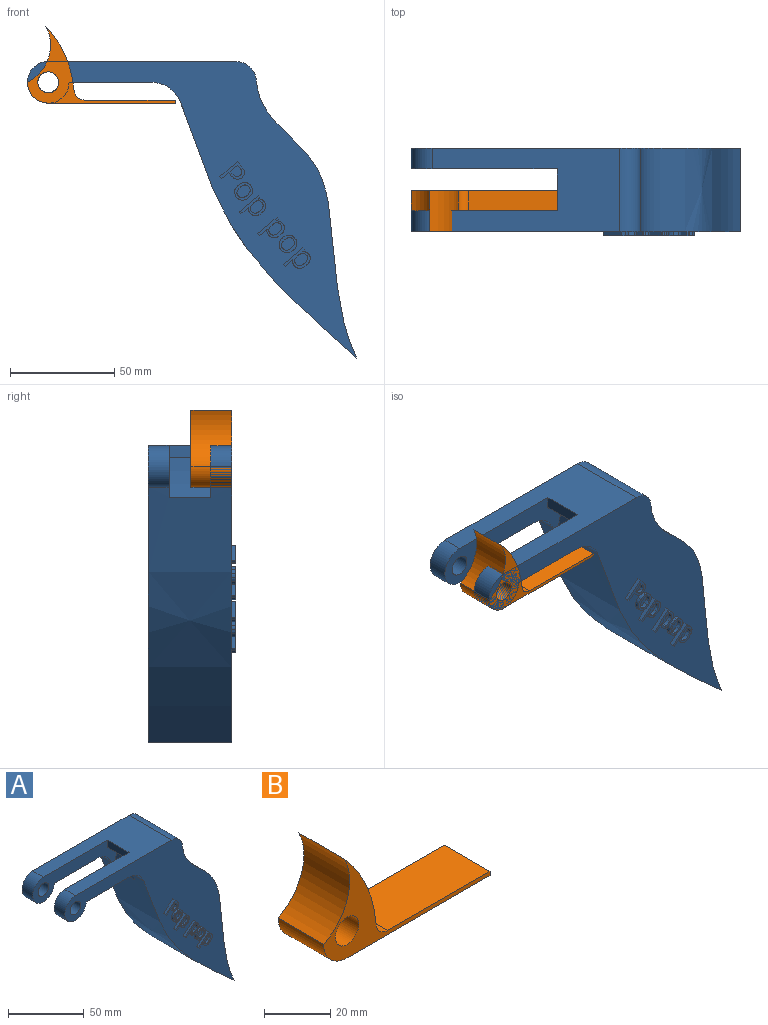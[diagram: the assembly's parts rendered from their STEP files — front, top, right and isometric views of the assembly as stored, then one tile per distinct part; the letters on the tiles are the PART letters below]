
ASSEMBLY  parts=2 mates=1
PART A: 155 faces, bbox 158.1x42x142.4 mm
  f0: cylinder r=70mm len=20mm, axis (0,1,0), area 390.4mm2, adj f1,f6,f12,f18
  f1: extruded ~122.5x84.4mm, area 5962.1mm2, adj f0,f2,f7,f10,f12,f13,f16,f18
  f2: extruded ~132.4x48.08mm, area 5806.9mm2, adj f1,f3,f7,f13
  f3: cylinder r=10mm len=40mm, axis (0,1,0), area 628.3mm2, adj f2,f4,f7,f13
  f4: plane 90x40mm, normal (0,0,1), area 2400mm2, adj f3,f5,f7,f8,f12,f13,f14,f18
  f5: plane 20x5.86mm, normal (-1,0,0), area 117.2mm2, adj f4,f6,f12,f18
  f6: plane 20x9.75mm, normal (0,0,-1), area 195.1mm2, adj f0,f5,f12,f18
  f7: plane 158.08x142.4mm, normal (0,1,0), area 6038mm2, adj f1,f2,f3,f4,f8,f9,f10,f11
  f8: cylinder r=10mm len=20mm, axis (0,1,0), area 471.2mm2, adj f4,f7,f9,f12
  f9: plane 39.58x10mm, normal (0,0,-1), area 395.8mm2, adj f7,f8,f10,f12
  f10: cylinder r=15mm len=14.11mm, axis (0,1,0), area 183.6mm2, adj f1,f7,f9,f12
  f11: cylinder r=5mm len=10mm, axis (0,1,0), area 314.2mm2, adj f7,f12
  f12: plane 79.75x24.84mm, normal (0,-1,0), area 889mm2, adj f0,f1,f4,f5,f6,f8,f9,f10
  f13: plane 158.08x142.4mm, normal (0,-1,0), area 5690.3mm2, adj f1,f2,f3,f4,f14,f15,f16,f17
  f14: cylinder r=10mm len=20mm, axis (0,-1,0), area 471.2mm2, adj f4,f13,f15,f18
  f15: plane 39.58x10mm, normal (0,0,-1), area 395.8mm2, adj f13,f14,f16,f18
  f16: cylinder r=15mm len=14.11mm, axis (0,-1,0), area 183.6mm2, adj f1,f13,f15,f18
  f17: cylinder r=5mm len=10mm, axis (0,-1,0), area 314.2mm2, adj f13,f18
  f18: plane 79.75x24.84mm, normal (0,1,0), area 889mm2, adj f0,f1,f4,f5,f6,f14,f15,f16
  f19: extruded ~5.36x2mm, area 12.2mm2, adj f13,f20,f33,f34
  f20: plane 2.24x2mm, normal (0.76,0,0.65), area 5.9mm2, adj f13,f19,f21,f34
  f21: plane 8.63x7.29mm, normal (-0.65,0,0.76), area 22.6mm2, adj f13,f20,f22,f34
  f22: plane 2x1mm, normal (-0.76,0,-0.65), area 2.6mm2, adj f13,f21,f23,f34
  f23: plane 3.39x2.87mm, normal (0.65,0,-0.76), area 8.9mm2, adj f13,f22,f24,f34
  f24: plane 2x1.02mm, normal (-0.76,0,-0.65), area 2.7mm2, adj f13,f23,f25,f34
  f25: extruded ~2.87x2mm, area 7.1mm2, adj f13,f24,f33,f34
  f26: plane 3.5x2.96mm, normal (0.65,0,-0.76), area 9.2mm2, adj f27,f32,f34,f35
  f27: plane 2x1.12mm, normal (-0.76,0,-0.65), area 2.9mm2, adj f26,f28,f34,f35
  f28: extruded ~2.1x2mm, area 4.8mm2, adj f27,f29,f34,f35
  f29: extruded ~2x1.64mm, area 3.8mm2, adj f28,f30,f34,f35
  f30: extruded ~2x1.89mm, area 4.1mm2, adj f29,f31,f34,f35
  f31: extruded ~2.06x2mm, area 5.3mm2, adj f30,f32,f34,f35
  f32: plane 2x0.9mm, normal (0.76,0,0.65), area 2.4mm2, adj f26,f31,f34,f35
  f33: extruded ~2.77x2mm, area 6mm2, adj f13,f19,f25,f34
  f34: plane 12.44x8.6mm, normal (0,-1,0), area 31.4mm2, adj f19,f20,f21,f22,f23,f24,f25,f26
  f35: plane 5.58x5.57mm, normal (0,-1,0), area 18.3mm2, adj f26,f27,f28,f29,f30,f31,f32
  f36: extruded ~2.86x2mm, area 6.9mm2, adj f13,f37,f52,f53
  f37: extruded ~2.92x2mm, area 6.3mm2, adj f13,f36,f38,f53
  f38: extruded ~2.74x2mm, area 6.4mm2, adj f13,f37,f39,f53
  f39: extruded ~3.13x2mm, area 6.9mm2, adj f13,f38,f40,f53
  f40: extruded ~2x1.87mm, area 4.8mm2, adj f13,f39,f41,f53
  f41: extruded ~2.03x2mm, area 4.2mm2, adj f13,f40,f42,f53
  f42: extruded ~2x1.89mm, area 4.2mm2, adj f13,f41,f43,f53
  f43: extruded ~2.75x2mm, area 6.4mm2, adj f13,f42,f52,f53
  f44: extruded ~2.3x2mm, area 5.2mm2, adj f45,f51,f53,f54
  f45: extruded ~2x1.86mm, area 4.3mm2, adj f44,f46,f53,f54
  f46: extruded ~2.01x2mm, area 4.4mm2, adj f45,f47,f53,f54
  f47: extruded ~2.08x2mm, area 5.2mm2, adj f46,f48,f53,f54
  f48: extruded ~2.31x2mm, area 5.2mm2, adj f47,f49,f53,f54
  f49: extruded ~2x1.88mm, area 4.3mm2, adj f48,f50,f53,f54
  f50: extruded ~2x2mm, area 4.3mm2, adj f49,f51,f53,f54
  f51: extruded ~2.09x2mm, area 5.2mm2, adj f44,f50,f53,f54
  f52: extruded ~3.14x2mm, area 7mm2, adj f13,f36,f43,f53
  f53: plane 8.81x8.61mm, normal (0,-1,0), area 27.5mm2, adj f36,f37,f38,f39,f40,f41,f42,f43
  f54: plane 6.52x6.2mm, normal (0,-1,0), area 28.1mm2, adj f44,f45,f46,f47,f48,f49,f50,f51
  f55: extruded ~2.55x2mm, area 5.9mm2, adj f13,f56,f79,f80
  f56: extruded ~3.08x2mm, area 6.9mm2, adj f13,f55,f57,f80
  f57: extruded ~2.78x2mm, area 6.8mm2, adj f13,f56,f58,f80
  f58: extruded ~2.73x2mm, area 5.9mm2, adj f13,f57,f59,f80
  f59: extruded ~2x1.21mm, area 3.1mm2, adj f13,f58,f60,f80
  f60: extruded ~2x1.51mm, area 3.1mm2, adj f13,f59,f61,f80
  f61: plane 2x0.05mm, normal (0.76,0,0.65), area 0.1mm2, adj f13,f60,f62,f80
  f62: plane 2x0.88mm, normal (0.75,0,-0.66), area 2.3mm2, adj f13,f61,f63,f80
  f63: plane 2x0.8mm, normal (0.76,0,0.65), area 2.1mm2, adj f13,f62,f64,f80
  f64: plane 9.37x7.92mm, normal (-0.65,0,0.76), area 24.5mm2, adj f13,f63,f65,f80
  f65: plane 2x0.98mm, normal (-0.76,0,-0.65), area 2.6mm2, adj f13,f64,f66,f80
  f66: plane 2.66x2.25mm, normal (0.65,0,-0.76), area 7mm2, adj f13,f65,f67,f80
  f67: extruded ~2x1.01mm, area 2.8mm2, adj f13,f66,f68,f80
  f68: plane 2x0.07mm, normal (-0.76,0,-0.65), area 0.2mm2, adj f13,f67,f69,f80
  f69: extruded ~2x1.48mm, area 3mm2, adj f13,f68,f79,f80
  f70: extruded ~2x1.88mm, area 4mm2, adj f71,f78,f80,f81
  f71: extruded ~2.04x2mm, area 5.1mm2, adj f70,f72,f80,f81
  f72: extruded ~2.27x2mm, area 5.1mm2, adj f71,f73,f80,f81
  f73: extruded ~2x1.79mm, area 4mm2, adj f72,f74,f80,f81
  f74: extruded ~2x1.95mm, area 4.3mm2, adj f73,f75,f80,f81
  f75: extruded ~2.1x2mm, area 5.3mm2, adj f74,f76,f80,f81
  f76: plane 2x0.22mm, normal (0.65,0,-0.76), area 0.6mm2, adj f75,f77,f80,f81
  f77: extruded ~2.13x2mm, area 4.8mm2, adj f76,f78,f80,f81
  f78: extruded ~2x1.76mm, area 4.2mm2, adj f70,f77,f80,f81
  f79: extruded ~2x1.35mm, area 3.1mm2, adj f13,f55,f69,f80
  f80: plane 13.02x9.84mm, normal (0,-1,0), area 35.5mm2, adj f55,f56,f57,f58,f59,f60,f61,f62
  f81: plane 6.45x6.12mm, normal (0,-1,0), area 26.8mm2, adj f70,f71,f72,f73,f74,f75,f76,f77
  f82: extruded ~2.55x2mm, area 5.9mm2, adj f13,f83,f106,f107
  f83: extruded ~3.08x2mm, area 6.9mm2, adj f13,f82,f84,f107
  f84: extruded ~2.78x2mm, area 6.8mm2, adj f13,f83,f85,f107
  f85: extruded ~2.73x2mm, area 5.9mm2, adj f13,f84,f86,f107
  f86: extruded ~2x1.21mm, area 3.1mm2, adj f13,f85,f87,f107
  f87: extruded ~2x1.51mm, area 3.1mm2, adj f13,f86,f88,f107
  f88: plane 2x0.05mm, normal (0.76,0,0.65), area 0.1mm2, adj f13,f87,f89,f107
  f89: plane 2x0.88mm, normal (0.75,0,-0.66), area 2.3mm2, adj f13,f88,f90,f107
  f90: plane 2x0.8mm, normal (0.76,0,0.65), area 2.1mm2, adj f13,f89,f91,f107
  f91: plane 9.37x7.92mm, normal (-0.65,0,0.76), area 24.5mm2, adj f13,f90,f92,f107
  f92: plane 2x0.98mm, normal (-0.76,0,-0.65), area 2.6mm2, adj f13,f91,f93,f107
  f93: plane 2.66x2.25mm, normal (0.65,0,-0.76), area 7mm2, adj f13,f92,f94,f107
  f94: extruded ~2x1.01mm, area 2.8mm2, adj f13,f93,f95,f107
  f95: plane 2x0.07mm, normal (-0.76,0,-0.65), area 0.2mm2, adj f13,f94,f96,f107
  f96: extruded ~2x1.48mm, area 3mm2, adj f13,f95,f106,f107
  f97: extruded ~2x1.88mm, area 4mm2, adj f98,f105,f107,f108
  f98: extruded ~2.04x2mm, area 5.1mm2, adj f97,f99,f107,f108
  f99: extruded ~2.27x2mm, area 5.1mm2, adj f98,f100,f107,f108
  f100: extruded ~2x1.79mm, area 4mm2, adj f99,f101,f107,f108
  f101: extruded ~2x1.95mm, area 4.3mm2, adj f100,f102,f107,f108
  f102: extruded ~2.1x2mm, area 5.3mm2, adj f101,f103,f107,f108
  f103: plane 2x0.22mm, normal (0.65,0,-0.76), area 0.6mm2, adj f102,f104,f107,f108
  f104: extruded ~2.13x2mm, area 4.8mm2, adj f103,f105,f107,f108
  f105: extruded ~2x1.76mm, area 4.2mm2, adj f97,f104,f107,f108
  f106: extruded ~2x1.35mm, area 3.1mm2, adj f13,f82,f96,f107
  f107: plane 13.02x9.84mm, normal (0,-1,0), area 35.5mm2, adj f82,f83,f84,f85,f86,f87,f88,f89
  f108: plane 6.45x6.12mm, normal (0,-1,0), area 26.8mm2, adj f97,f98,f99,f100,f101,f102,f103,f104
  f109: extruded ~2.86x2mm, area 6.9mm2, adj f13,f110,f125,f126
  f110: extruded ~2.92x2mm, area 6.3mm2, adj f13,f109,f111,f126
  f111: extruded ~2.74x2mm, area 6.4mm2, adj f13,f110,f112,f126
  f112: extruded ~3.13x2mm, area 6.9mm2, adj f13,f111,f113,f126
  f113: extruded ~2x1.87mm, area 4.8mm2, adj f13,f112,f114,f126
  f114: extruded ~2.03x2mm, area 4.2mm2, adj f13,f113,f115,f126
  f115: extruded ~2x1.89mm, area 4.2mm2, adj f13,f114,f116,f126
  f116: extruded ~2.75x2mm, area 6.4mm2, adj f13,f115,f125,f126
  f117: extruded ~2.3x2mm, area 5.2mm2, adj f118,f124,f126,f127
  f118: extruded ~2x1.86mm, area 4.3mm2, adj f117,f119,f126,f127
  f119: extruded ~2.01x2mm, area 4.4mm2, adj f118,f120,f126,f127
  f120: extruded ~2.08x2mm, area 5.2mm2, adj f119,f121,f126,f127
  f121: extruded ~2.31x2mm, area 5.2mm2, adj f120,f122,f126,f127
  f122: extruded ~2x1.88mm, area 4.3mm2, adj f121,f123,f126,f127
  f123: extruded ~2x2mm, area 4.3mm2, adj f122,f124,f126,f127
  f124: extruded ~2.09x2mm, area 5.2mm2, adj f117,f123,f126,f127
  f125: extruded ~3.14x2mm, area 7mm2, adj f13,f109,f116,f126
  f126: plane 8.81x8.61mm, normal (0,-1,0), area 27.5mm2, adj f109,f110,f111,f112,f113,f114,f115,f116
  f127: plane 6.52x6.2mm, normal (0,-1,0), area 28.1mm2, adj f117,f118,f119,f120,f121,f122,f123,f124
  f128: extruded ~2.55x2mm, area 5.9mm2, adj f13,f129,f152,f153
  f129: extruded ~3.08x2mm, area 6.9mm2, adj f13,f128,f130,f153
  f130: extruded ~2.78x2mm, area 6.8mm2, adj f13,f129,f131,f153
  f131: extruded ~2.73x2mm, area 5.9mm2, adj f13,f130,f132,f153
  f132: extruded ~2x1.21mm, area 3.1mm2, adj f13,f131,f133,f153
  f133: extruded ~2x1.51mm, area 3.1mm2, adj f13,f132,f134,f153
  f134: plane 2x0.05mm, normal (0.76,0,0.65), area 0.1mm2, adj f13,f133,f135,f153
  f135: plane 2x0.88mm, normal (0.75,0,-0.66), area 2.3mm2, adj f13,f134,f136,f153
  f136: plane 2x0.8mm, normal (0.76,0,0.65), area 2.1mm2, adj f13,f135,f137,f153
  f137: plane 9.37x7.92mm, normal (-0.65,0,0.76), area 24.5mm2, adj f13,f136,f138,f153
  f138: plane 2x0.98mm, normal (-0.76,0,-0.65), area 2.6mm2, adj f13,f137,f139,f153
  f139: plane 2.66x2.25mm, normal (0.65,0,-0.76), area 7mm2, adj f13,f138,f140,f153
  f140: extruded ~2x1.01mm, area 2.8mm2, adj f13,f139,f141,f153
  f141: plane 2x0.07mm, normal (-0.76,0,-0.65), area 0.2mm2, adj f13,f140,f142,f153
  f142: extruded ~2x1.48mm, area 3mm2, adj f13,f141,f152,f153
  f143: extruded ~2x1.88mm, area 4mm2, adj f144,f151,f153,f154
  f144: extruded ~2.04x2mm, area 5.1mm2, adj f143,f145,f153,f154
  f145: extruded ~2.27x2mm, area 5.1mm2, adj f144,f146,f153,f154
  f146: extruded ~2x1.79mm, area 4mm2, adj f145,f147,f153,f154
  f147: extruded ~2x1.95mm, area 4.3mm2, adj f146,f148,f153,f154
  f148: extruded ~2.1x2mm, area 5.3mm2, adj f147,f149,f153,f154
  f149: plane 2x0.22mm, normal (0.65,0,-0.76), area 0.6mm2, adj f148,f150,f153,f154
  f150: extruded ~2.13x2mm, area 4.8mm2, adj f149,f151,f153,f154
  f151: extruded ~2x1.76mm, area 4.2mm2, adj f143,f150,f153,f154
  f152: extruded ~2x1.35mm, area 3.1mm2, adj f13,f128,f142,f153
  f153: plane 13.02x9.84mm, normal (0,-1,0), area 35.5mm2, adj f128,f129,f130,f131,f132,f133,f134,f135
  f154: plane 6.45x6.12mm, normal (0,-1,0), area 26.8mm2, adj f143,f144,f145,f146,f147,f148,f149,f150
PART B: 10 faces, bbox 71x19.5x37 mm
  f0: cylinder r=20mm len=27.04mm, axis (0,1,0), area 617.8mm2, adj f1,f6,f8,f9
  f1: cylinder r=10mm len=19.5mm, axis (0,1,0), area 306.3mm2, adj f0,f2,f8,f9
  f2: plane 61x19.5mm, normal (0,0,-1), area 1189.5mm2, adj f1,f3,f8,f9
  f3: plane 19.5x1.5mm, normal (1,0,0), area 29.2mm2, adj f2,f4,f8,f9
  f4: plane 43.63x19.5mm, normal (0,0,1), area 850.7mm2, adj f3,f5,f8,f9
  f5: cylinder r=5mm len=19.5mm, axis (0,1,0), area 145.6mm2, adj f4,f6,f8,f9
  f6: cylinder r=51.51mm len=30.93mm, axis (0,1,0), area 670.4mm2, adj f0,f5,f8,f9
  f7: cylinder r=5mm len=19.5mm, axis (0,1,0), area 612.6mm2, adj f8,f9
  f8: plane 71x37.04mm, normal (0,-1,0), area 426.1mm2, adj f0,f1,f2,f3,f4,f5,f6,f7
  f9: plane 71x37.04mm, normal (0,1,0), area 426.1mm2, adj f0,f1,f2,f3,f4,f5,f6,f7
PLACE A t=(-68.8,9.93,35.34)mm
PLACE B t=(-68.8,-10.57,15.34)mm
MATE revolute B.f7 <-> A.f8  axis (0,-1,0) through (-68.8,-30.07,25.34)mm
